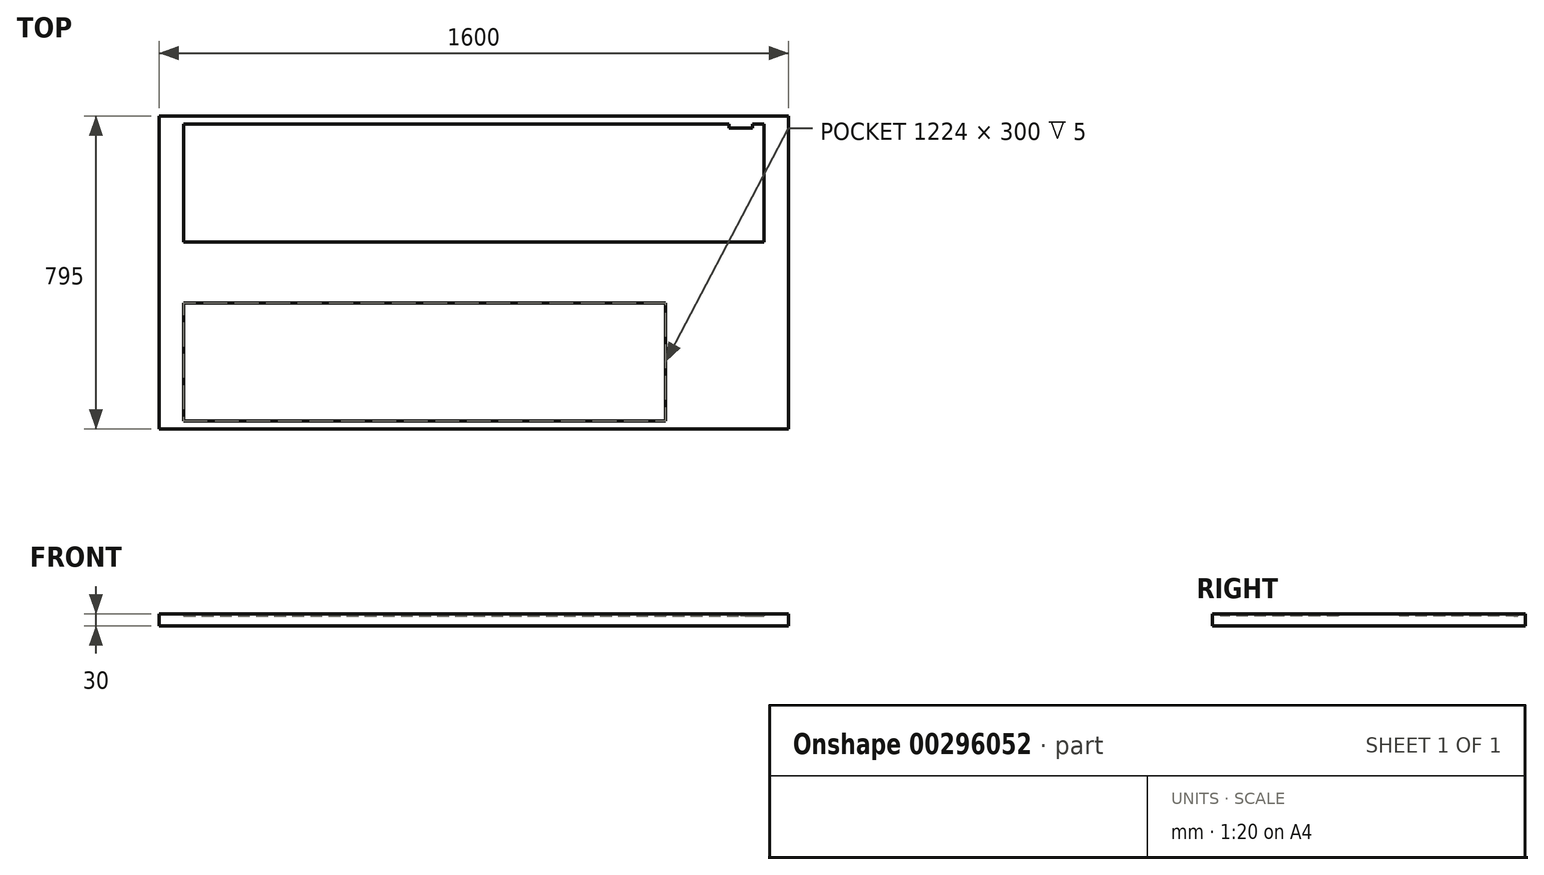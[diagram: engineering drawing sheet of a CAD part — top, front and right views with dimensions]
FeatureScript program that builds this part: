
annotation { "Feature Type Name" : "Feature", "Feature Type Description" : "" }
export const myFeature = defineFeature(function(context is Context, id is Id, definition is map)
    precondition{}
    {
        {
            var Q0;
            Q0=qCreatedBy(makeId("Top.planeOp"),FACE);
            var sketch = newSketch(context, id + "F0", { "sketchPlane" : qUnion([Q0])});
            skLineSegment(sketch, "E0.bottom", {"start": v(800, 397.5) * mm, "end": v(-800, 397.5) * mm});
            skLineSegment(sketch, "E0.top", {"start": v(800, -397.5) * mm, "end": v(-800, -397.5) * mm});
            skLineSegment(sketch, "E0.left", {"start": v(800, 397.5) * mm, "end": v(800, -397.5) * mm});
            skLineSegment(sketch, "E0.right", {"start": v(-800, 397.5) * mm, "end": v(-800, -397.5) * mm});
            skPoint(sketch, "E0.middle", {"position": v(0, 0) * mm});
            skLineSegment(sketch, "E1", {"start": v(-800, 377.5) * mm, "end": v(800, 377.5) * mm});
            skLineSegment(sketch, "E2", {"start": v(-800, -377.5) * mm, "end": v(800, -377.5) * mm});
            skLineSegment(sketch, "E3", {"start": v(-800, -77.5) * mm, "end": v(800, -77.5) * mm});
            skLineSegment(sketch, "E4", {"start": v(-800, 77.5) * mm, "end": v(800, 77.5) * mm});
            skLineSegment(sketch, "E5", {"start": v(-737, 397.5) * mm, "end": v(-737, -397.5) * mm});
            skLineSegment(sketch, "E6", {"start": v(737, 397.5) * mm, "end": v(737, -397.5) * mm});
            skLineSegment(sketch, "E7", {"start": v(708, 397.5) * mm, "end": v(708, 367.5) * mm});
            skLineSegment(sketch, "E8", {"start": v(708, 367.5) * mm, "end": v(648, 367.5) * mm});
            skLineSegment(sketch, "E9", {"start": v(648, 367.5) * mm, "end": v(648, 397.5) * mm});
            skLineSegment(sketch, "E10", {"start": v(487, -77.5) * mm, "end": v(487, -397.5) * mm});
            skSolve(sketch);
        }
        {
            var Q0;
            {var subQ0=sQuery(id+"F0.wireOp",EDGE,"E0.top");Q0=makeQuery(id+"F0.imprint","IMPRINT",FACE,{"disambiguationData":[TD([[makeQuery(id+"F0.imprint","IMPRINT",EDGE,{"derivedFrom":subQ0}),-1.0]])]});}
            var Q1;
            {var subQ0=sQuery(id+"F0.wireOp",EDGE,"E5");var subQ1=sQuery(id+"F0.wireOp",EDGE,"E0.bottom");var subQ2=makeQuery(id+"F0.imprint","INTERSECT",VERTEX,{"derivedFrom":[subQ1,subQ0]});Q1=makeQuery(id+"F0.imprint","IMPRINT",FACE,{"disambiguationData":[TD([[makeQuery(id+"F0.imprint","IMPRINT",EDGE,{"disambiguationData":[TD([[subQ2,1.0]])],"derivedFrom":subQ1}),1.0]])]});}
            var Q2;
            {var subQ0=sQuery(id+"F0.wireOp",EDGE,"E7");var subQ1=sQuery(id+"F0.wireOp",EDGE,"E0.bottom");var subQ2=makeQuery(id+"F0.imprint","INTERSECT",VERTEX,{"derivedFrom":[subQ1,subQ0]});Q2=makeQuery(id+"F0.imprint","IMPRINT",FACE,{"disambiguationData":[TD([[makeQuery(id+"F0.imprint","IMPRINT",EDGE,{"disambiguationData":[TD([[subQ2,-1.0]])],"derivedFrom":subQ1}),1.0]])]});}
            var Q3;
            {var subQ5=sQuery(id+"F0.wireOp",EDGE,"E8");Q3=makeQuery(id+"F0.imprint","IMPRINT",FACE,{"disambiguationData":[TD([[makeQuery(id+"F0.imprint","IMPRINT",EDGE,{"derivedFrom":subQ5}),-1.0]])]});}
            var Q4;
            {var subQ0=sQuery(id+"F0.wireOp",EDGE,"E6");var subQ1=sQuery(id+"F0.wireOp",EDGE,"E0.bottom");var subQ2=makeQuery(id+"F0.imprint","INTERSECT",VERTEX,{"derivedFrom":[subQ1,subQ0]});Q4=makeQuery(id+"F0.imprint","IMPRINT",FACE,{"disambiguationData":[TD([[makeQuery(id+"F0.imprint","IMPRINT",EDGE,{"disambiguationData":[TD([[subQ2,-1.0]])],"derivedFrom":subQ1}),1.0]])]});}
            var Q5;
            {var subQ0=sQuery(id+"F0.wireOp",EDGE,"E0.left");var subQ1=sQuery(id+"F0.wireOp",EDGE,"E0.bottom");var subQ2=makeQuery(id+"F0.imprint","INTERSECT",VERTEX,{"derivedFrom":[subQ1,subQ0]});Q5=makeQuery(id+"F0.imprint","IMPRINT",FACE,{"disambiguationData":[TD([[makeQuery(id+"F0.imprint","IMPRINT",EDGE,{"disambiguationData":[TD([[subQ2,-1.0]])],"derivedFrom":subQ1}),1.0]])]});}
            var Q6;
            {var subQ0=sQuery(id+"F0.wireOp",EDGE,"E1");var subQ1=sQuery(id+"F0.wireOp",EDGE,"E0.left");var subQ2=makeQuery(id+"F0.imprint","INTERSECT",VERTEX,{"derivedFrom":[subQ1,subQ0]});Q6=makeQuery(id+"F0.imprint","IMPRINT",FACE,{"disambiguationData":[TD([[makeQuery(id+"F0.imprint","IMPRINT",EDGE,{"disambiguationData":[TD([[subQ2,-1.0]])],"derivedFrom":subQ1}),-1.0]])]});}
            var Q7;
            {var subQ1=sQuery(id+"F0.wireOp",EDGE,"E3");var subQ7=makeQuery(id+"F0.imprint","INTERSECT",VERTEX,{"derivedFrom":[subQ1,sQuery(id+"F0.wireOp",EDGE,"E10")]});Q7=makeQuery(id+"F0.imprint","IMPRINT",FACE,{"disambiguationData":[TD([[makeQuery(id+"F0.imprint","IMPRINT",EDGE,{"disambiguationData":[TD([[subQ7,1.0]])],"derivedFrom":subQ1}),1.0]])]});}
            var Q8;
            {var subQ0=sQuery(id+"F0.wireOp",EDGE,"E0.right");var subQ1=sQuery(id+"F0.wireOp",EDGE,"E0.bottom");var subQ2=makeQuery(id+"F0.imprint","INTERSECT",VERTEX,{"derivedFrom":[subQ1,subQ0]});Q8=makeQuery(id+"F0.imprint","IMPRINT",FACE,{"disambiguationData":[TD([[makeQuery(id+"F0.imprint","IMPRINT",EDGE,{"disambiguationData":[TD([[subQ2,1.0]])],"derivedFrom":subQ1}),1.0]])]});}
            var Q9;
            {var subQ0=sQuery(id+"F0.wireOp",EDGE,"E1");var subQ1=sQuery(id+"F0.wireOp",EDGE,"E0.right");var subQ2=makeQuery(id+"F0.imprint","INTERSECT",VERTEX,{"derivedFrom":[subQ1,subQ0]});Q9=makeQuery(id+"F0.imprint","IMPRINT",FACE,{"disambiguationData":[TD([[makeQuery(id+"F0.imprint","IMPRINT",EDGE,{"disambiguationData":[TD([[subQ2,-1.0]])],"derivedFrom":subQ1}),1.0]])]});}
            var Q10;
            {var subQ0=sQuery(id+"F0.wireOp",EDGE,"E3");var subQ1=sQuery(id+"F0.wireOp",EDGE,"E0.right");var subQ2=makeQuery(id+"F0.imprint","INTERSECT",VERTEX,{"derivedFrom":[subQ1,subQ0]});Q10=makeQuery(id+"F0.imprint","IMPRINT",FACE,{"disambiguationData":[TD([[makeQuery(id+"F0.imprint","IMPRINT",EDGE,{"disambiguationData":[TD([[subQ2,1.0]])],"derivedFrom":subQ1}),1.0]])]});}
            var Q11;
            {var subQ0=sQuery(id+"F0.wireOp",EDGE,"E2");var subQ1=sQuery(id+"F0.wireOp",EDGE,"E0.right");var subQ2=makeQuery(id+"F0.imprint","INTERSECT",VERTEX,{"derivedFrom":[subQ1,subQ0]});Q11=makeQuery(id+"F0.imprint","IMPRINT",FACE,{"disambiguationData":[TD([[makeQuery(id+"F0.imprint","IMPRINT",EDGE,{"disambiguationData":[TD([[subQ2,1.0]])],"derivedFrom":subQ1}),1.0]])]});}
            var Q12;
            {var subQ0=sQuery(id+"F0.wireOp",EDGE,"E3");var subQ1=sQuery(id+"F0.wireOp",EDGE,"E0.left");var subQ2=makeQuery(id+"F0.imprint","INTERSECT",VERTEX,{"derivedFrom":[subQ1,subQ0]});Q12=makeQuery(id+"F0.imprint","IMPRINT",FACE,{"disambiguationData":[TD([[makeQuery(id+"F0.imprint","IMPRINT",EDGE,{"disambiguationData":[TD([[subQ2,1.0]])],"derivedFrom":subQ1}),-1.0]])]});}
            var Q13;
            {var subQ0=sQuery(id+"F0.wireOp",EDGE,"E2");var subQ1=sQuery(id+"F0.wireOp",EDGE,"E0.left");var subQ2=makeQuery(id+"F0.imprint","INTERSECT",VERTEX,{"derivedFrom":[subQ1,subQ0]});Q13=makeQuery(id+"F0.imprint","IMPRINT",FACE,{"disambiguationData":[TD([[makeQuery(id+"F0.imprint","IMPRINT",EDGE,{"disambiguationData":[TD([[subQ2,1.0]])],"derivedFrom":subQ1}),-1.0]])]});}
            var Q14;
            {var subQ0=sQuery(id+"F0.wireOp",EDGE,"E10");var subQ1=sQuery(id+"F0.wireOp",EDGE,"E2");var subQ2=makeQuery(id+"F0.imprint","INTERSECT",VERTEX,{"derivedFrom":[subQ1,subQ0]});Q14=makeQuery(id+"F0.imprint","IMPRINT",FACE,{"disambiguationData":[TD([[makeQuery(id+"F0.imprint","IMPRINT",EDGE,{"disambiguationData":[TD([[subQ2,-1.0]])],"derivedFrom":subQ1}),1.0]])]});}
            extrude(context, id + "F1", {"entities" : qUnion([Q0, Q1, Q2, Q3, Q4, Q5, Q6, Q7, Q8, Q9, Q10, Q11, Q12, Q13, Q14]), "depth" : 30 * mm, "offsetDistance" : 25 * mm});
        }
        {
            var Q0;
            {var subQ5=sQuery(id+"F0.wireOp",EDGE,"E8");Q0=makeQuery(id+"F0.imprint","IMPRINT",FACE,{"disambiguationData":[TD([[makeQuery(id+"F0.imprint","IMPRINT",EDGE,{"derivedFrom":subQ5}),1.0]])]});}
            var Q1;
            {var subQ0=sQuery(id+"F0.wireOp",EDGE,"E5");var subQ1=sQuery(id+"F0.wireOp",EDGE,"E2");var subQ2=makeQuery(id+"F0.imprint","INTERSECT",VERTEX,{"derivedFrom":[subQ1,subQ0]});Q1=makeQuery(id+"F0.imprint","IMPRINT",FACE,{"disambiguationData":[TD([[makeQuery(id+"F0.imprint","IMPRINT",EDGE,{"disambiguationData":[TD([[subQ2,-1.0]])],"derivedFrom":subQ1}),1.0]])]});}
            extrude(context, id + "F2", {"entities" : qUnion([Q0, Q1]), "operationType" : NewBodyOperationType.ADD, "depth" : 25 * mm, "offsetDistance" : 25 * mm});
        }
    });
